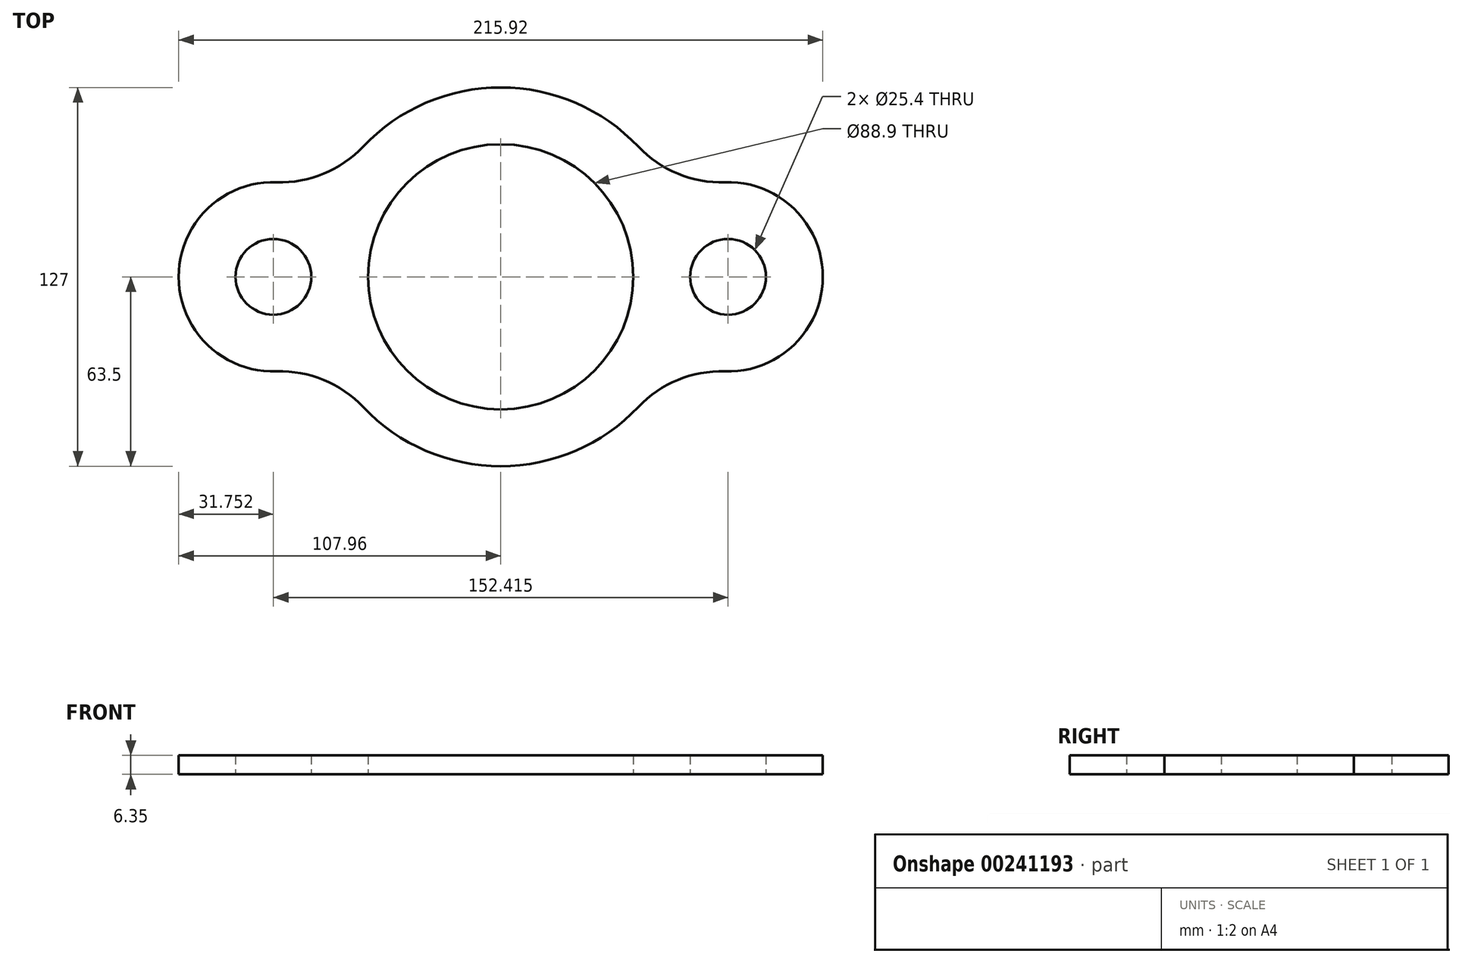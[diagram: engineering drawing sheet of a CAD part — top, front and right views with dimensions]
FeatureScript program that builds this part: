
annotation { "Feature Type Name" : "Feature", "Feature Type Description" : "" }
export const myFeature = defineFeature(function(context is Context, id is Id, definition is map)
    precondition{}
    {
        {
            var Q0;
            Q0=qCreatedBy(makeId("Top.planeOp"),FACE);
            var sketch = newSketch(context, id + "F0", { "sketchPlane" : qUnion([Q0])});
            skCircle(sketch, "E0", {"center": v(0, 0) * mm, "radius": 44.45 * mm});
            skCircle(sketch, "E1", {"center": v(76.2, 0) * mm, "radius": 12.7 * mm});
            skCircle(sketch, "E2.MirrorC", {"center": v(-76.2, 0) * mm, "radius": 12.7 * mm});
            skArc(sketch, "E3", {"start": v(-75.12, 31.73) * mm, "mid": v(-107.96, 0) * mm, "end": v(-75.12, -31.73) * mm});
            skArc(sketch, "E4.MirrorCS", {"start": v(75.12, 31.73) * mm, "mid": v(107.96, 0) * mm, "end": v(75.12, -31.73) * mm});
            skArc(sketch, "E5", {"start": v(46.14, 43.63) * mm, "mid": v(0, 63.5) * mm, "end": v(-46.14, 43.63) * mm});
            skArc(sketch, "E6.MirrorCS", {"start": v(46.14, -43.63) * mm, "mid": v(0, -63.5) * mm, "end": v(-46.14, -43.63) * mm});
            skPoint(sketch, "E7.visualSharp", {"position": v(-57.95, 25.97) * mm});
            skArc(sketch, "E7.filletArc", {"start": v(-75.12, 31.73) * mm, "mid": v(-59.35, 34.56) * mm, "end": v(-46.14, 43.63) * mm});
            skPoint(sketch, "E8.visualSharp", {"position": v(-57.95, -25.97) * mm});
            skArc(sketch, "E8.filletArc", {"start": v(-46.14, -43.63) * mm, "mid": v(-59.35, -34.56) * mm, "end": v(-75.12, -31.73) * mm});
            skPoint(sketch, "E9.visualSharp", {"position": v(57.95, 25.97) * mm});
            skArc(sketch, "E9.filletArc", {"start": v(46.14, 43.63) * mm, "mid": v(59.35, 34.56) * mm, "end": v(75.12, 31.73) * mm});
            skPoint(sketch, "E10.visualSharp", {"position": v(57.95, -25.97) * mm});
            skArc(sketch, "E10.filletArc", {"start": v(75.12, -31.73) * mm, "mid": v(59.35, -34.56) * mm, "end": v(46.14, -43.63) * mm});
            skSolve(sketch);
        }
        {
            var Q0;
            Q0 = qSketchRegion(id + "F0", true);
            extrude(context, id + "F1", {"entities" : qUnion([Q0]), "depth" : 6.35 * mm});
        }
    });
